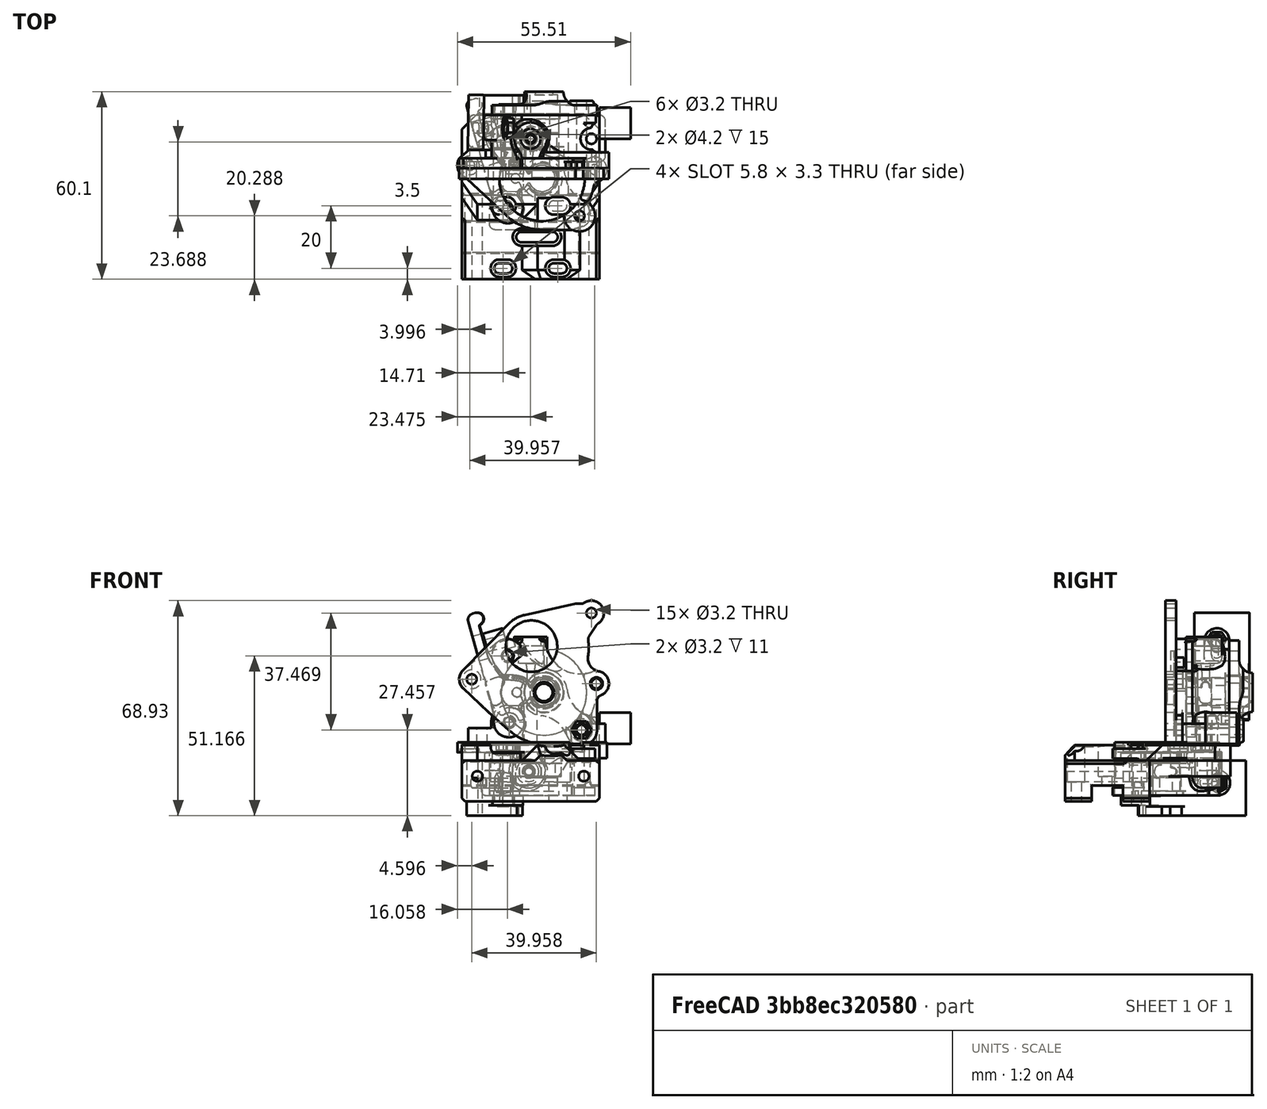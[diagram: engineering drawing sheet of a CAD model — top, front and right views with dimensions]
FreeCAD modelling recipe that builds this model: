
FCSTD DOCUMENT  (FreeCAD 0.18R16146 (Git))
Label: extrudort-standalone
License: All rights reserved
LicenseURL: http://en.wikipedia.org/wiki/All_rights_reserved
objects: Part::Cylinder×15, Part::Cut×14, Part::Feature×13, Part::MultiFuse×6, Part::Box×6, Part::Fillet×2, App::Part×1, Part::Chamfer×1, Mesh::Feature×1
note: 57 computed .brp shape members not serialized (recipe doc carries the construction recipe); baked Part::Feature solids carry a one-line shape summary decoded from their .brp

FEATURE [Part::Feature] Part__Feature  label="HextrodORT_E3D_BODY"
  shape: bbox 47.96 x 38.43 x 17 mm, 159 faces (baked)
FEATURE [Part::Feature] Part__Feature001  label="HextrudORT_TENSION_ARM v1"
  Placement = pos=(-0.165448,1.6043,-3.4e-13) rot=(0,0,1;0rad)
  shape: bbox 18.28 x 39.94 x 20.1 mm, 56 faces (baked)
FEATURE [App::Part] HextrudORT_BODY_Blank_v1  label="HextrudORT_BODY_Blank v1"
  Group = -> [Part__Feature,Part__Feature001]
  Origin = -> Origin
FEATURE [Part::Cylinder] Cylinder
  Angle = 360
  AttacherType = Attacher::AttachEngine3D
  Height = 10
  Placement = pos=(4.25,4e-15,16.5) rot=(1,0,0;1.5708rad)
  Radius = 13.7
FEATURE [Part::Feature] Part__Feature002  label="HextrodORT_E3D_BODY001"
  Placement = pos=(0.6,-8.9,29.19) rot=(1,0,0;1.5708rad)
  shape: bbox 47.96 x 17 x 38.43 mm, 159 faces (baked)
FEATURE [Part::Cylinder] Cylinder001
  Angle = 360
  AttacherType = Attacher::AttachEngine3D
  Height = 2.6
  Placement = pos=(-7.41,-6.8,28.16) rot=(1,0,0;1.5708rad)
  Radius = 4
FEATURE [Part::Cut] Cut
  Base = -> Cylinder001
  Tool = -> Cylinder
FEATURE [Part::Cylinder] Cylinder002
  Angle = 360
  AttacherType = Attacher::AttachEngine3D
  Height = 6
  Placement = pos=(-7.41,-3.4,28.16) rot=(1,0,0;1.5708rad)
  Radius = 2
FEATURE [Part::MultiFuse] Fusion
  Shapes = -> [Cut,Part__Feature002]
FEATURE [Part::Cut] Cut001
  Base = -> Fusion
  Tool = -> Cylinder002
FEATURE [Part::Cylinder] Cylinder003
  Angle = 360
  AttacherType = Attacher::AttachEngine3D
  Height = 6.5
  Placement = pos=(-14.227,3.6,31.4454) rot=(0,1,0;1.30097rad)
  Radius = 3.55
FEATURE [Part::Cylinder] Cylinder004
  Angle = 360
  AttacherType = Attacher::AttachEngine3D
  Height = 6.5
  Placement = pos=(-14.227,3.6,31.4454) rot=(0,1,0;1.30097rad)
  Radius = 2
FEATURE [Part::Chamfer] Chamfer
  Base = -> Cylinder003
  Edges = 1 edges: [Edge3 r1=1 r2=1.9]
FEATURE [Part::MultiFuse] Fusion001
  Shapes = -> [Chamfer,Cut001]
FEATURE [Part::Cut] Cut002
  Base = -> Fusion001
  Tool = -> Cylinder004
FEATURE [Part::Feature] Part__Feature003  label="HextrudORT_BLANK_CarriageBackPlate_Body v3"
  Placement = pos=(-6.9,19.05,-10.44) rot=(0,0,1;3.14159rad)
  shape: bbox 47.96 x 5.5 x 46.44 mm, 54 faces (baked)
FEATURE [Part::Feature] Part__Feature023  label="HextrudORT_COVER v2"
  Placement = pos=(0.604522,-8.90284,29.1689) rot=(1,0,0;1.5708rad)
  shape: bbox 34.87 x 10.47 x 34.87 mm, 33 faces (baked)
FEATURE [Part::Feature] Part__Feature011  label="HextrudORT_TENSION_ARM v002"
  Placement = pos=(0.189269,-9.13883,30.7709) rot=(0.999977,-0.004789,-0.004789;1.57082rad)
  shape: bbox 18.28 x 20.27 x 39.94 mm, 56 faces (baked)
FEATURE [Part::Cylinder] Cylinder005
  Angle = 360
  AttacherType = Attacher::AttachEngine3D
  Height = 5.5
  Placement = pos=(16.29,-7.4,4.48) rot=(1,0,0;1.5708rad)
  Radius = 3.55
FEATURE [Part::Cylinder] Cylinder006
  Angle = 360
  AttacherType = Attacher::AttachEngine3D
  Height = 5.5
  Placement = pos=(16.29,-7.4,4.48) rot=(1,0,0;1.5708rad)
  Radius = 2
FEATURE [Part::MultiFuse] Fusion002
  Shapes = -> [Part__Feature003,Cylinder005]
FEATURE [Part::Cut] Cut003
  Base = -> Fusion002
  Tool = -> Cylinder006
FEATURE [Part::Cylinder] Cylinder007
  Angle = 360
  AttacherType = Attacher::AttachEngine3D
  Height = 10
  Placement = pos=(0.3,-8.4,31.3) rot=(1,0,0;1.5708rad)
  Radius = 8.25
FEATURE [Part::Cut] Cut004
  Base = -> Cut003
  Tool = -> Cylinder007
FEATURE [Part::Cylinder] Cylinder008
  Angle = 360
  AttacherType = Attacher::AttachEngine3D
  Height = 10
  Placement = pos=(19.5,0,0) rot=(0,0,1;0rad)
  Radius = 1.65
FEATURE [Part::Cylinder] Cylinder009
  Angle = 360
  AttacherType = Attacher::AttachEngine3D
  Height = 10
  Placement = pos=(-15.5,2.25,5) rot=(0,0,1;0rad)
  Radius = 3.5
FEATURE [Part::Box] Box  label="Cube"
  AttacherType = Attacher::AttachEngine3D
  Height = 6.5
  Length = 10.5
  Placement = pos=(13.5,-7.4,0) rot=(0,0,1;0rad)
  Width = 15
FEATURE [Part::Fillet] Fillet
  Base = -> Box
  Edges = 2 edges r=2: [Edge5,Edge7]
FEATURE [Part::Cylinder] Cylinder010
  Angle = 360
  AttacherType = Attacher::AttachEngine3D
  Height = 10
  Placement = pos=(19.5,0,6.5) rot=(0,0,1;0rad)
  Radius = 3.5
FEATURE [Part::Cylinder] Cylinder011
  Angle = 360
  AttacherType = Attacher::AttachEngine3D
  Height = 27
  Placement = pos=(16.29,-13.53,4.47) rot=(-1,0,0;1.5708rad)
  Radius = 1.7
FEATURE [Part::Cut] Cut005
  Base = -> Fillet
  Tool = -> Cylinder011
FEATURE [Part::MultiFuse] Fusion003
  Shapes = -> [Cylinder010,Cylinder008]
FEATURE [Part::MultiFuse] Fusion004
  Shapes = -> [Cut005,Cut002]
FEATURE [Part::Cut] Cut006
  Base = -> Fusion004
  Tool = -> Fusion003
FEATURE [Part::Box] Box001  label="Cube001"
  AttacherType = Attacher::AttachEngine3D
  Height = 5
  Length = 10
  Placement = pos=(-20,-2.9,0) rot=(0,0,1;0rad)
  Width = 10.5
FEATURE [Part::Fillet] Fillet001
  Base = -> Box001
  Edges = 2 edges r=2: [Edge1,Edge3]
FEATURE [Part::Cylinder] Cylinder012
  Angle = 360
  AttacherType = Attacher::AttachEngine3D
  Height = 10
  Placement = pos=(-15.5,2.25,0) rot=(0,0,1;0rad)
  Radius = 1.65
FEATURE [Part::Cut] Cut007
  Base = -> Fillet001
  Tool = -> Cylinder012
FEATURE [Part::MultiFuse] Fusion005
  Shapes = -> [Cut007,Cut006]
FEATURE [Part::Cut] Cut008
  Base = -> Fusion005
  Tool = -> Cylinder009
FEATURE [Mesh::Feature] sherpa_mini_b3_mockup_1_  label="sherpa_mini_b3_mockup(1)"
  Placement = pos=(25.6,-30.5,-8) rot=(0,0.707107,0.707107;3.14159rad)
FEATURE [Part::Cylinder] Cylinder013
  Angle = 360
  AttacherType = Attacher::AttachEngine3D
  Height = 7
  Placement = pos=(-6.74,0.6,7) rot=(-1,0,0;1.5708rad)
  Radius = 2
FEATURE [Part::Cut] Cut009
  Base = -> Cut008
  Tool = -> Cylinder013
FEATURE [Part::Cylinder] Cylinder014
  Angle = 360
  AttacherType = Attacher::AttachEngine3D
  Height = 10
  Placement = pos=(21.1,-3.91,19.33) rot=(1,0,0;1.5708rad)
  Radius = 2
FEATURE [Part::Cut] Cut010
  Base = -> Cut004
  Tool = -> Cylinder014
FEATURE [Part::Box] Box002  label="Cube002"
  AttacherType = Attacher::AttachEngine3D
  Height = 2
  Length = 15
  Placement = pos=(6,-17,-2) rot=(0,0,1;0rad)
  Width = 31
FEATURE [Part::Box] Box003  label="Cube003"
  AttacherType = Attacher::AttachEngine3D
  Height = 2
  Length = 15
  Placement = pos=(6,-17,-2) rot=(0,0,1;0rad)
  Width = 31
FEATURE [Part::Box] Box004  label="Cube004"
  AttacherType = Attacher::AttachEngine3D
  Height = 2
  Length = 15
  Placement = pos=(6,-17,-2) rot=(0,0,1;0rad)
  Width = 31
FEATURE [Part::Cut] Cut011
  Base = -> Cut010
  Tool = -> Box002
FEATURE [Part::Cut] Cut012
  Base = -> Cut009
  Tool = -> Box003
FEATURE [Part::Feature] Part__Feature023001  label="HextrudORT_COVER v003"
  Placement = pos=(0,0,0.01) rot=(0,0,1;0rad)
  shape: bbox 34.87 x 10.47 x 34.87 mm, 33 faces (baked)
FEATURE [Part::Cut] Cut013
  Base = -> Part__Feature023001
  Tool = -> Box004
FEATURE [Part::Feature] Part__Feature023002  label="HextrudORT_TENSION_ARM v003"
  Placement = pos=(0.189269,-9.13883,30.7709) rot=(0.999977,-0.004789,-0.004789;1.57082rad)
  shape: bbox 18.28 x 20.27 x 39.94 mm, 56 faces (baked)
FEATURE [Part::Feature] Part__Feature023002001  label="HextrudORT_TENSION_ARM v004"
  shape: bbox 18.28 x 20.27 x 39.94 mm, 56 faces (baked)
FEATURE [Part::Feature] Cut013001  label="Cut014"
  shape: bbox 34.87 x 10.47 x 34.87 mm, 35 faces (baked)
FEATURE [Part::Feature] Cut011001  label="Cut016"
  shape: bbox 47.96 x 5.504 x 45.93 mm, 52 faces (baked)
FEATURE [Part::Feature] Body001
  Placement = pos=(0,0,-10.5) rot=(0,0,1;3.14159rad)
  shape: bbox 44.1 x 53 x 18 mm, 98 faces (baked)
FEATURE [Part::Box] Box005  label="Cube005"
  AttacherType = Attacher::AttachEngine3D
  Height = 10
  Length = 10
  Placement = pos=(22.05,0,0) rot=(0,0,1;0rad)
  Width = 10
FEATURE [Part::Feature] Fillet002001  label="Fillet003"
  shape: bbox 47.96 x 17 x 37.45 mm, 170 faces (baked)
